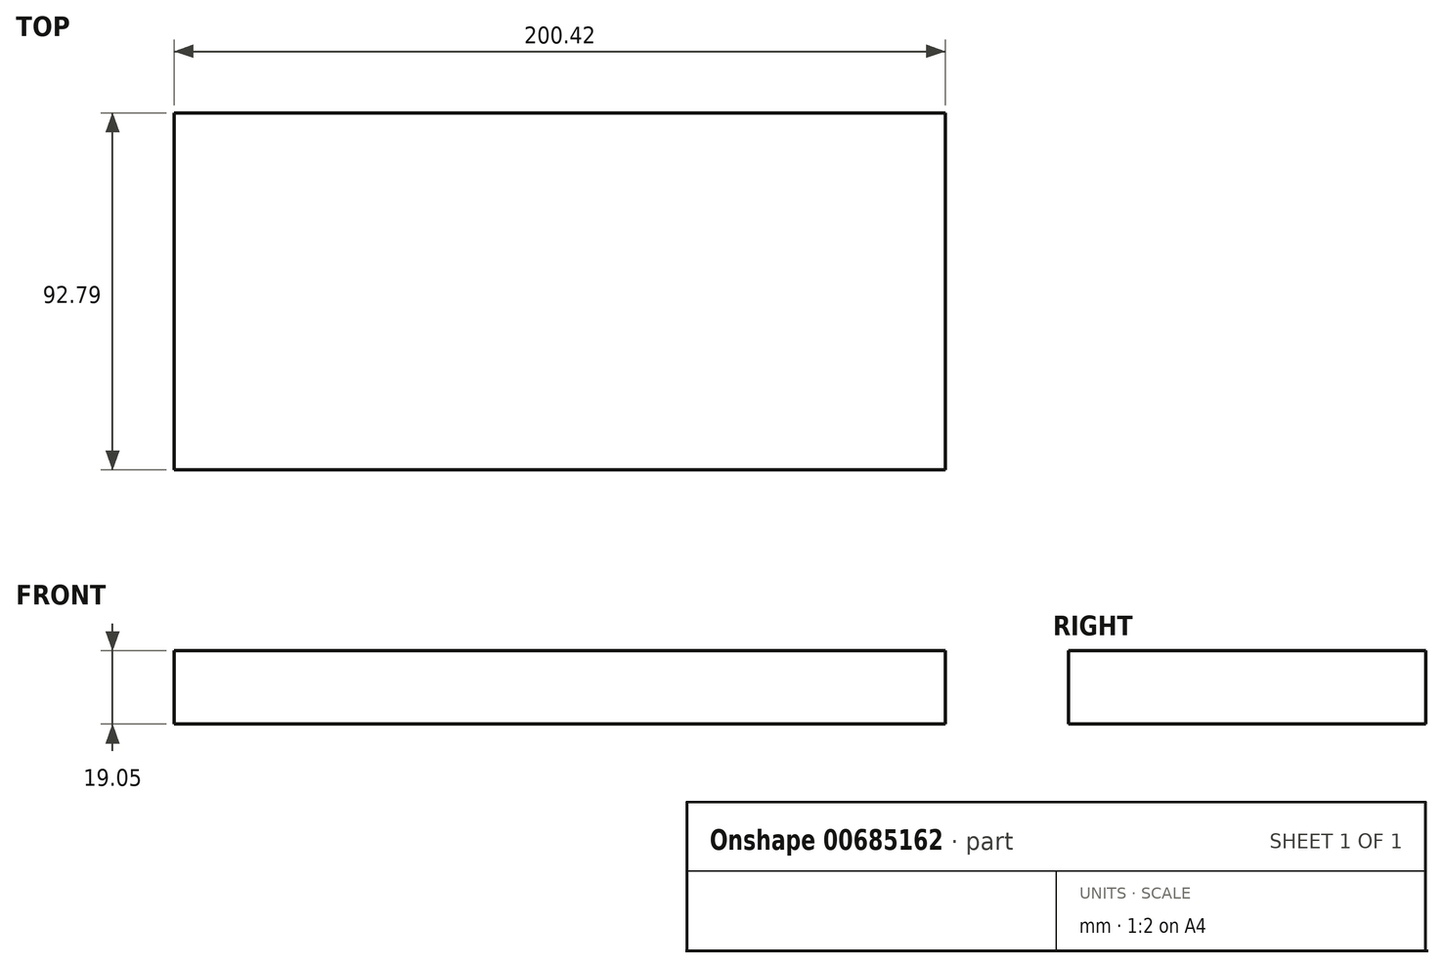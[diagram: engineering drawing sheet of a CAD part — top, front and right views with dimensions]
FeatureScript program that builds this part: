
annotation { "Feature Type Name" : "Feature", "Feature Type Description" : "" }
export const myFeature = defineFeature(function(context is Context, id is Id, definition is map)
    precondition{}
    {
        {
            var Q0;
            Q0=qCreatedBy(makeId("Top.planeOp"),FACE);
            var sketch = newSketch(context, id + "F0", { "sketchPlane" : qUnion([Q0])});
            skLineSegment(sketch, "E0.bottom", {"start": v(-60.76, 67.86) * mm, "end": v(139.66, 67.86) * mm});
            skLineSegment(sketch, "E0.top", {"start": v(-60.76, -24.93) * mm, "end": v(139.66, -24.93) * mm});
            skLineSegment(sketch, "E0.left", {"start": v(-60.76, 67.86) * mm, "end": v(-60.76, -24.93) * mm});
            skLineSegment(sketch, "E0.right", {"start": v(139.66, 67.86) * mm, "end": v(139.66, -24.93) * mm});
            skSolve(sketch);
        }
        {
            var Q0;
            Q0=makeQuery(id+"F0.imprint","IMPRINT",FACE,{"disambiguationData":[TD([[makeQuery(id+"F0.imprint","IMPRINT",EDGE,{"derivedFrom":sQuery(id+"F0.wireOp",EDGE,"E0.bottom")}),-1.0]])]});
            extrude(context, id + "F1", {"entities" : qUnion([Q0]), "depth" : 19.05 * mm, "offsetDistance" : 25.4 * mm});
        }
    });
